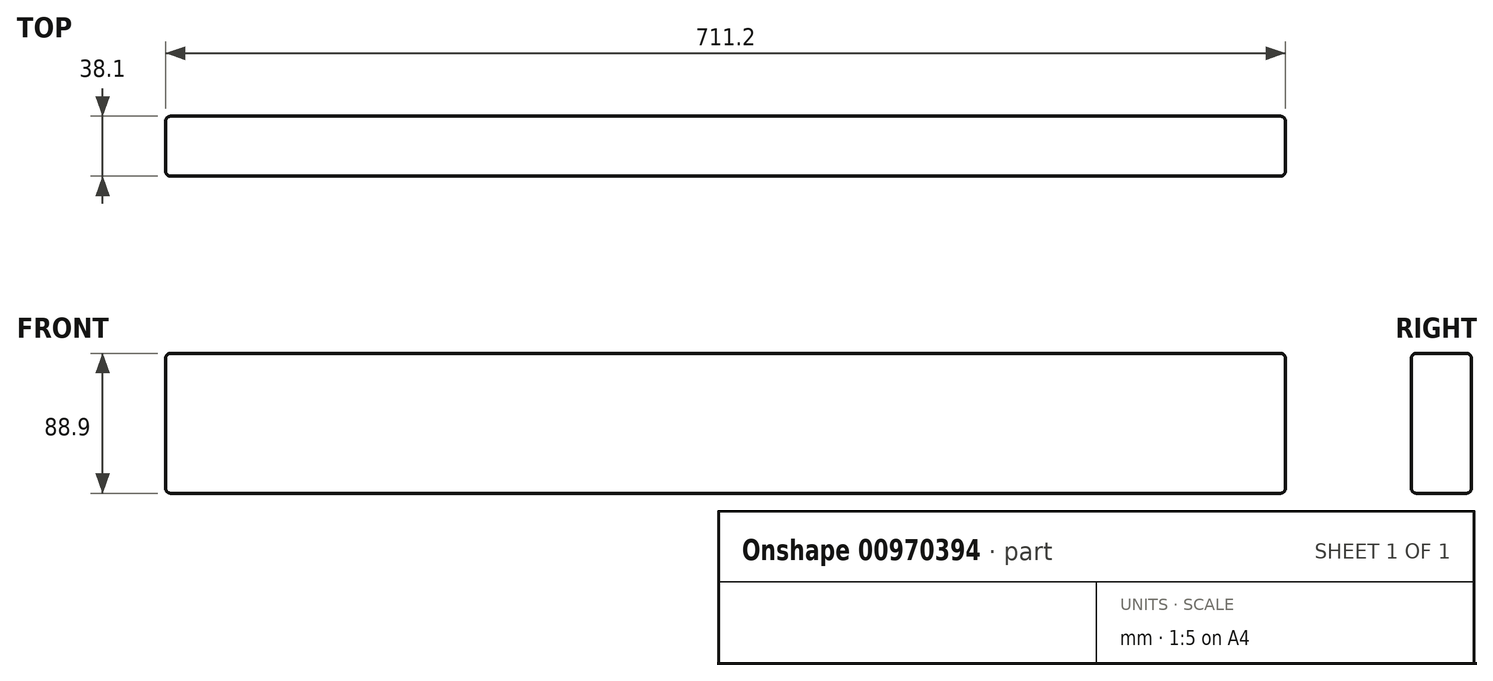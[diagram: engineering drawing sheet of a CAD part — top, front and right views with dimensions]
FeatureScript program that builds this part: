
annotation { "Feature Type Name" : "Feature", "Feature Type Description" : "" }
export const myFeature = defineFeature(function(context is Context, id is Id, definition is map)
    precondition{}
    {
        {
            var Q0;
            Q0=qCreatedBy(makeId("Front.planeOp"),FACE);
            var sketch = newSketch(context, id + "F0", { "sketchPlane" : qUnion([Q0])});
            skLineSegment(sketch, "E0.bottom", {"start": v(-711.2, 88.9) * mm, "end": v(0, 88.9) * mm});
            skLineSegment(sketch, "E0.top", {"start": v(-711.2, 0) * mm, "end": v(0, 0) * mm});
            skLineSegment(sketch, "E0.left", {"start": v(-711.2, 88.9) * mm, "end": v(-711.2, 0) * mm});
            skLineSegment(sketch, "E0.right", {"start": v(0, 88.9) * mm, "end": v(0, 0) * mm});
            skSolve(sketch);
        }
        {
            var Q0;
            Q0=makeQuery(id+"F0.imprint","IMPRINT",FACE,{"disambiguationData":[TD([[makeQuery(id+"F0.imprint","IMPRINT",EDGE,{"derivedFrom":sQuery(id+"F0.wireOp",EDGE,"E0.bottom")}),-1.0]])]});
            extrude(context, id + "F1", {"entities" : qUnion([Q0]), "depth" : 38.1 * mm, "offsetDistance" : 25.4 * mm});
        }
        {
            var Q0;
            Q0=makeQuery(id+"F1.opExtrude","CAP_EDGE",EDGE,{"disambiguationData":[OSD([sQuery(id+"F0.wireOp",EDGE,"E0.left")])],"isStart":true});
            var Q1;
            Q1=makeQuery(id+"F1.opExtrude","CAP_EDGE",EDGE,{"disambiguationData":[OSD([sQuery(id+"F0.wireOp",EDGE,"E0.left")])],"isStart":false});
            var Q2;
            Q2=makeQuery(id+"F1.opExtrude","SWEPT_EDGE",EDGE,{"disambiguationData":[OSD([sQuery(id+"F0.wireOp",EDGE,"E0.top"),sQuery(id+"F0.wireOp",EDGE,"E0.left")])]});
            var Q3;
            Q3=makeQuery(id+"F1.opExtrude","CAP_EDGE",EDGE,{"disambiguationData":[OSD([sQuery(id+"F0.wireOp",EDGE,"E0.bottom")])],"isStart":true});
            var Q4;
            Q4=makeQuery(id+"F1.opExtrude","SWEPT_EDGE",EDGE,{"disambiguationData":[OSD([sQuery(id+"F0.wireOp",EDGE,"E0.bottom"),sQuery(id+"F0.wireOp",EDGE,"E0.left")])]});
            var Q5;
            Q5=makeQuery(id+"F1.opExtrude","CAP_EDGE",EDGE,{"disambiguationData":[OSD([sQuery(id+"F0.wireOp",EDGE,"E0.bottom")])],"isStart":false});
            var Q6;
            Q6=makeQuery(id+"F1.opExtrude","CAP_EDGE",EDGE,{"disambiguationData":[OSD([sQuery(id+"F0.wireOp",EDGE,"E0.top")])],"isStart":false});
            var Q7;
            Q7=makeQuery(id+"F1.opExtrude","SWEPT_EDGE",EDGE,{"disambiguationData":[OSD([sQuery(id+"F0.wireOp",EDGE,"E0.bottom"),sQuery(id+"F0.wireOp",EDGE,"E0.right")])]});
            var Q8;
            Q8=makeQuery(id+"F1.opExtrude","CAP_EDGE",EDGE,{"disambiguationData":[OSD([sQuery(id+"F0.wireOp",EDGE,"E0.right")])],"isStart":true});
            var Q9;
            Q9=makeQuery(id+"F1.opExtrude","CAP_EDGE",EDGE,{"disambiguationData":[OSD([sQuery(id+"F0.wireOp",EDGE,"E0.right")])],"isStart":false});
            var Q10;
            Q10=makeQuery(id+"F1.opExtrude","SWEPT_EDGE",EDGE,{"disambiguationData":[OSD([sQuery(id+"F0.wireOp",EDGE,"E0.top"),sQuery(id+"F0.wireOp",EDGE,"E0.right")])]});
            var Q11;
            Q11=makeQuery(id+"F1.opExtrude","CAP_EDGE",EDGE,{"disambiguationData":[OSD([sQuery(id+"F0.wireOp",EDGE,"E0.top")])],"isStart":true});
            fillet(context, id + "F2", {"entities" : qUnion([Q0, Q1, Q2, Q3, Q4, Q5, Q6, Q7, Q8, Q9, Q10, Q11]), "radius" : 3.17 * mm, "tangentPropagation" : true, "allowEdgeOverflow" : false});
        }
    });
